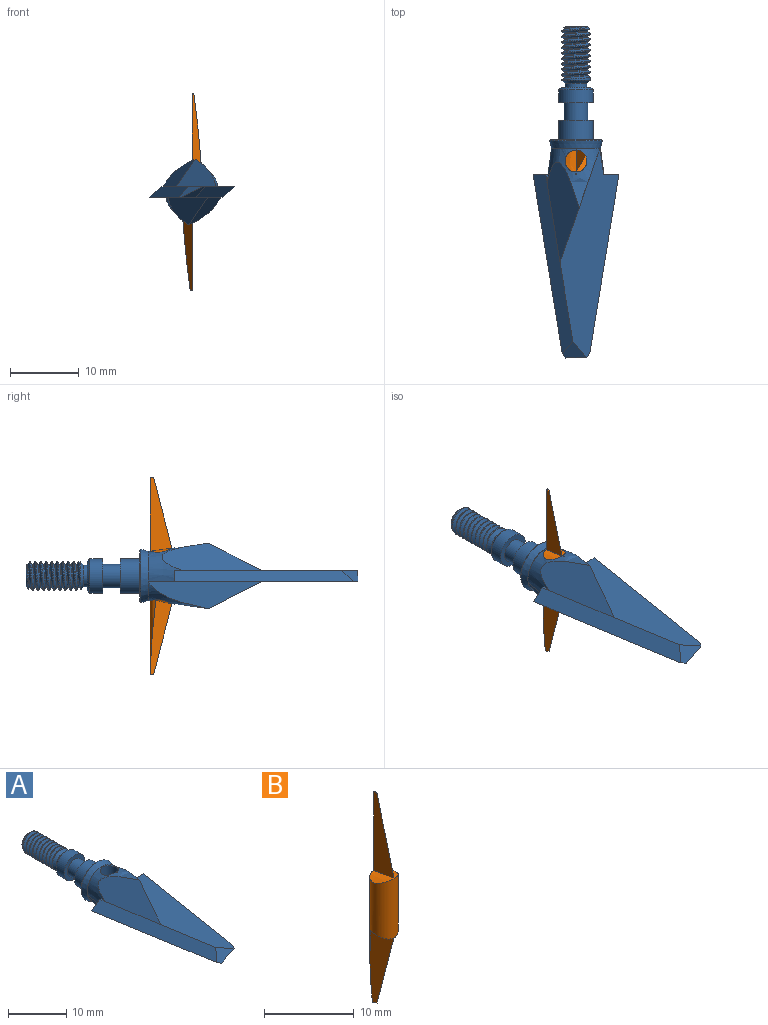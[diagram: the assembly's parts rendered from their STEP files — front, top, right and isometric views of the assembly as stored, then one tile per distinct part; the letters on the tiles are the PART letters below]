
ASSEMBLY  parts=2 mates=1
PART A: 45 faces, bbox 12.5x285.9x9.6 mm
  f0: cylinder r=2.08mm len=7.37mm, axis (0,-1,0), area 16.8mm2, adj f1,f6,f41,f42,f44
  f1: cone r=1.58mm half-angle=47.1deg, axis (0,1,0), area 7mm2, adj f0,f7,f41,f42
  f2: cylinder r=2.54mm len=5.08mm, axis (0,-1,0), area 29.9mm2, adj f4,f8
  f3: plane 4.32x4.32mm, normal (0,1,0), area 6.8mm2, adj f4,f7
  f4: cone r=2.16mm half-angle=45deg, axis (0,-1,0), area 8mm2, adj f2,f3
  f5: plane 3.15x3.15mm, normal (0,1,0), area 7.8mm2, adj f6
  f6: cone r=1.57mm half-angle=45deg, axis (0,-1,0), area 4.1mm2, adj f0,f5,f42,f43,f44
  f7: cylinder r=1.58mm len=3.16mm, axis (0,1,0), area 5.4mm2, adj f1,f3
  f8: plane 5.08x5.08mm, normal (0,-1,0), area 11mm2, adj f2,f10
  f9: plane 5.08x5.08mm, normal (0,1,0), area 11mm2, adj f10,f40
  f10: cylinder r=1.72mm len=3.44mm, axis (0,1,0), area 27.4mm2, adj f8,f9
  f11: plane 3.52x2.44mm, normal (-0.42,-0.34,0.84), area 5.5mm2, adj f12,f16,f20,f27
  f12: plane 3.52x2.44mm, normal (0.42,-0.34,-0.84), area 5.5mm2, adj f11,f13,f20,f27
  f13: plane 26.09x5.78mm, normal (0.63,-0.1,-0.77), area 60.4mm2, adj f12,f20,f22,f23,f24,f27
  f14: plane 0.05x0.05mm, normal (0,-1,0), area 0mm2, adj f21,f22,f27
  f15: plane 0.05x0.04mm, normal (0,-1,0), area 0mm2, adj f20,f28,f29
  f16: plane 26.09x5.78mm, normal (-0.63,-0.1,0.77), area 60.4mm2, adj f11,f20,f25,f26,f27,f29
  f17: bspline ~259.18x0.33mm, area 0mm2, adj f18,f19,f30,f34
  f18: plane 0.1x0.09mm, normal (0,1,0), area 0mm2, adj f17,f19,f34
  f19: bspline ~259.18x0.34mm, area 0mm2, adj f17,f18,f30,f34
  f20: plane 30.49x8.58mm, normal (0,0,1), area 127.8mm2, adj f11,f12,f13,f15,f16,f24,f28,f34
  f21: plane 16.51x5.76mm, normal (-0.94,-0.33,0), area 41.4mm2, adj f14,f22,f27,f34
  f22: plane 14.5x4.64mm, normal (0.7,-0.11,-0.71), area 52.2mm2, adj f13,f14,f21,f34
  f23: plane 1.25x0.38mm, normal (0,0,-1), area 0.2mm2, adj f13,f24,f34
  f24: plane 2.22x1.52mm, normal (0,1,0), area 1.9mm2, adj f13,f20,f23,f34
  f25: plane 1.25x0.38mm, normal (0,0,1), area 0.2mm2, adj f16,f26,f35
  f26: plane 2.22x1.52mm, normal (0,1,0), area 1.9mm2, adj f16,f25,f27,f35
  f27: plane 30.48x8.58mm, normal (0,0,-1), area 127.8mm2, adj f11,f12,f13,f14,f16,f21,f26,f35
  f28: plane 16.51x5.76mm, normal (0.94,-0.33,0), area 41.4mm2, adj f15,f20,f29,f35
  f29: plane 14.5x4.64mm, normal (-0.7,-0.11,0.71), area 52.1mm2, adj f15,f16,f28,f35
  f30: cylinder r=1.59mm len=8.08mm, axis (0,0,-1), area 72.7mm2, adj f17,f19,f31,f33,f34,f35
  f31: bspline ~259.18x0.33mm, area 0mm2, adj f30,f32,f33,f35
  f32: plane 0.1x0.09mm, normal (0,1,0), area 0mm2, adj f31,f33,f35
  f33: bspline ~259.18x0.34mm, area 0mm2, adj f30,f31,f32,f35
  f34: cone r=3.56mm half-angle=8deg, axis (0,-1,0), area 34.2mm2, adj f17,f18,f19,f20,f21,f22,f23,f24
  f35: cone r=3.56mm half-angle=8deg, axis (0,-1,0), area 34.1mm2, adj f25,f26,f27,f28,f29,f30,f31,f32
  f36: plane 7.15x7.15mm, normal (0,-1,0), area 0.4mm2, adj f34,f35,f37
  f37: cone r=3.94mm half-angle=16deg, axis (0,1,0), area 27mm2, adj f36,f38
  f38: torus R=3.77mm, axis (0,1,0), area 5.7mm2, adj f37,f39
  f39: plane 7.54x7.54mm, normal (0,1,0), area 24.3mm2, adj f38,f40
  f40: cylinder r=2.54mm len=5.08mm, axis (0,-1,0), area 45.1mm2, adj f9,f39
  f41: plane 0.54x0.46mm, normal (0,0,-1), area 0.1mm2, adj f0,f1,f42,f43,f44
  f42: bspline ~8.2x4.16mm, area 60.3mm2, adj f0,f1,f6,f41,f43
  f43: cylinder r=1.62mm len=7.93mm, axis (0,1,0), area 15.6mm2, adj f6,f41,f42,f44
  f44: bspline ~8.07x4.81mm, area 57.7mm2, adj f0,f6,f41,f43
PART B: 11 faces, bbox 3.4x3.2x28.6 mm
  f0: cylinder r=1.59mm len=28.58mm, axis (0,0,-1), area 93.6mm2, adj f1,f2,f3,f4,f5,f6,f7,f8
  f1: plane 0.51x0.27mm, normal (0,0,-1), area 0.1mm2, adj f0,f3,f9
  f2: plane 0.51x0.27mm, normal (0,0,1), area 0.1mm2, adj f0,f4,f7
  f3: plane 10.69x3.18mm, normal (1,0,0), area 19.6mm2, adj f0,f1,f6,f9
  f4: plane 10.69x3.18mm, normal (-1,0,0), area 19.6mm2, adj f0,f2,f5,f7
  f5: cone r=3.56mm half-angle=8deg, axis (0,-1,0), area 4.1mm2, adj f0,f4
  f6: cone r=3.56mm half-angle=8deg, axis (0,-1,0), area 4.1mm2, adj f0,f3
  f7: plane 10.85x3.15mm, normal (0.87,-0.48,0.13), area 18.9mm2, adj f0,f2,f4,f8
  f8: cone r=3.56mm half-angle=8deg, axis (0,-1,0), area 1.6mm2, adj f0,f7
  f9: plane 10.85x3.15mm, normal (-0.87,-0.48,-0.13), area 18.9mm2, adj f0,f1,f3,f10
  f10: cone r=3.56mm half-angle=8deg, axis (0,-1,0), area 1.6mm2, adj f0,f9
PLACE A at identity fixed
PLACE B t=(0,3.81,0)mm
MATE cylindrical A.f30 <-> B.f0  axis (0,0,-1) through (0,1.96,0)mm
